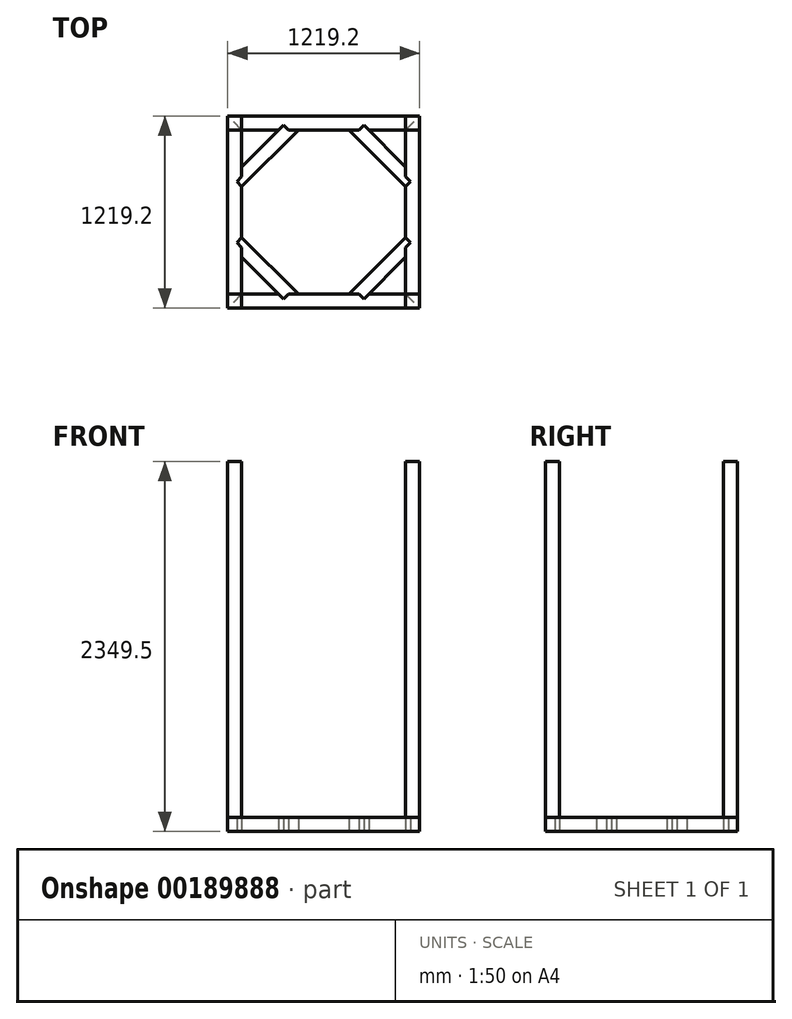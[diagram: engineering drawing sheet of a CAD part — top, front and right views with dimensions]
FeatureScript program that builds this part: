
annotation { "Feature Type Name" : "Feature", "Feature Type Description" : "" }
export const myFeature = defineFeature(function(context is Context, id is Id, definition is map)
    precondition{}
    {
        {
            var Q0;
            Q0=qCreatedBy(makeId("Top.planeOp"),FACE);
            var sketch = newSketch(context, id + "F0", { "sketchPlane" : qUnion([Q0])});
            skLineSegment(sketch, "E0.bottom", {"start": v(609.6, 609.6) * mm, "end": v(-609.6, 609.6) * mm});
            skLineSegment(sketch, "E0.top", {"start": v(609.6, -609.6) * mm, "end": v(-609.6, -609.6) * mm});
            skLineSegment(sketch, "E0.left", {"start": v(609.6, 609.6) * mm, "end": v(609.6, -609.6) * mm});
            skLineSegment(sketch, "E0.right", {"start": v(-609.6, 609.6) * mm, "end": v(-609.6, -609.6) * mm});
            skPoint(sketch, "E0.middle", {"position": v(0, 0) * mm});
            skLineSegment(sketch, "E1.0", {"start": v(520.7, 520.7) * mm, "end": v(287.21, 520.7) * mm});
            skLineSegment(sketch, "E1.1", {"start": v(520.7, 520.7) * mm, "end": v(520.7, 224.35) * mm});
            skLineSegment(sketch, "E1.2", {"start": v(520.7, -520.7) * mm, "end": v(287.21, -520.7) * mm});
            skLineSegment(sketch, "E1.3", {"start": v(-520.7, 520.7) * mm, "end": v(-520.7, 224.35) * mm});
            skLineSegment(sketch, "E2", {"start": v(-520.7, 520.7) * mm, "end": v(-609.6, 609.6) * mm});
            skLineSegment(sketch, "E3", {"start": v(520.7, 520.7) * mm, "end": v(609.6, 609.6) * mm});
            skLineSegment(sketch, "E4", {"start": v(520.7, -520.7) * mm, "end": v(609.6, -609.6) * mm});
            skLineSegment(sketch, "E5", {"start": v(-520.7, -520.7) * mm, "end": v(-609.6, -609.6) * mm});
            skLineSegment(sketch, "E6", {"start": v(-161.49, -520.7) * mm, "end": v(-520.7, -161.49) * mm});
            skLineSegment(sketch, "E7", {"start": v(-287.21, -520.7) * mm, "end": v(-520.7, -287.21) * mm});
            skLineSegment(sketch, "E8", {"start": v(-520.7, -161.49) * mm, "end": v(-552.13, -192.92) * mm});
            skLineSegment(sketch, "E9", {"start": v(-552.13, -192.92) * mm, "end": v(-520.7, -224.35) * mm});
            skLineSegment(sketch, "E10", {"start": v(-287.21, -520.7) * mm, "end": v(-255.78, -552.13) * mm});
            skLineSegment(sketch, "E11", {"start": v(-255.78, -552.13) * mm, "end": v(-224.35, -520.7) * mm});
            skLineSegment(sketch, "E12.trimOffspring", {"start": v(-287.21, -520.7) * mm, "end": v(-520.7, -520.7) * mm});
            skLineSegment(sketch, "E13.trimOffspring", {"start": v(-520.7, -224.35) * mm, "end": v(-520.7, -520.7) * mm});
            skLineSegment(sketch, "E14", {"start": v(0, 609.6) * mm, "end": v(0, -609.6) * mm, "construction": true});
            skLineSegment(sketch, "E15", {"start": v(609.6, 0) * mm, "end": v(-609.6, 0) * mm, "construction": true});
            skLineSegment(sketch, "E16.MirrorCS", {"start": v(161.49, -520.7) * mm, "end": v(520.7, -161.49) * mm});
            skLineSegment(sketch, "E17.MirrorCS", {"start": v(287.21, -520.7) * mm, "end": v(520.7, -287.21) * mm});
            skLineSegment(sketch, "E18.MirrorCS", {"start": v(552.13, -192.92) * mm, "end": v(520.7, -224.35) * mm});
            skLineSegment(sketch, "E19.MirrorCS", {"start": v(520.7, -161.49) * mm, "end": v(552.13, -192.92) * mm});
            skLineSegment(sketch, "E20.MirrorCS", {"start": v(255.78, -552.13) * mm, "end": v(224.35, -520.7) * mm});
            skLineSegment(sketch, "E21.MirrorCS", {"start": v(287.21, -520.7) * mm, "end": v(255.78, -552.13) * mm});
            skLineSegment(sketch, "E22.trimOffspring", {"start": v(224.35, -520.7) * mm, "end": v(-224.35, -520.7) * mm});
            skLineSegment(sketch, "E23.trimOffspring", {"start": v(520.7, -224.35) * mm, "end": v(520.7, -520.7) * mm});
            skLineSegment(sketch, "E24.MirrorCS", {"start": v(161.49, 520.7) * mm, "end": v(520.7, 161.49) * mm});
            skLineSegment(sketch, "E25.MirrorCS", {"start": v(520.7, 161.49) * mm, "end": v(552.13, 192.92) * mm});
            skLineSegment(sketch, "E26.MirrorCS", {"start": v(552.13, 192.92) * mm, "end": v(520.7, 224.35) * mm});
            skLineSegment(sketch, "E27.MirrorCS", {"start": v(287.21, 520.7) * mm, "end": v(520.7, 287.21) * mm});
            skLineSegment(sketch, "E28.MirrorCS", {"start": v(255.78, 552.13) * mm, "end": v(224.35, 520.7) * mm});
            skLineSegment(sketch, "E29.MirrorCS", {"start": v(287.21, 520.7) * mm, "end": v(255.78, 552.13) * mm});
            skLineSegment(sketch, "E30.MirrorCS", {"start": v(-161.49, 520.7) * mm, "end": v(-520.7, 161.49) * mm});
            skLineSegment(sketch, "E31.MirrorCS", {"start": v(-287.21, 520.7) * mm, "end": v(-520.7, 287.21) * mm});
            skLineSegment(sketch, "E32.MirrorCS", {"start": v(-552.13, 192.92) * mm, "end": v(-520.7, 224.35) * mm});
            skLineSegment(sketch, "E33.MirrorCS", {"start": v(-520.7, 161.49) * mm, "end": v(-552.13, 192.92) * mm});
            skLineSegment(sketch, "E34.MirrorCS", {"start": v(-287.21, 520.7) * mm, "end": v(-255.78, 552.13) * mm});
            skLineSegment(sketch, "E35.MirrorCS", {"start": v(-255.78, 552.13) * mm, "end": v(-224.35, 520.7) * mm});
            skLineSegment(sketch, "E36.trimOffspring", {"start": v(-287.21, 520.7) * mm, "end": v(-520.7, 520.7) * mm});
            skLineSegment(sketch, "E37.trimOffspring", {"start": v(-520.7, 161.49) * mm, "end": v(-520.7, -161.49) * mm});
            skLineSegment(sketch, "E38.trimOffspring", {"start": v(224.35, 520.7) * mm, "end": v(-224.35, 520.7) * mm});
            skLineSegment(sketch, "E39.trimOffspring", {"start": v(520.7, 161.49) * mm, "end": v(520.7, -161.49) * mm});
            skSolve(sketch);
        }
        {
            var Q0;
            Q0=makeQuery(id+"F0.imprint","IMPRINT",FACE,{"disambiguationData":[TD([[makeQuery(id+"F0.imprint","IMPRINT",EDGE,{"derivedFrom":sQuery(id+"F0.wireOp",EDGE,"E0.bottom")}),1.0]])]});
            extrude(context, id + "F1", {"entities" : qUnion([Q0]), "depth" : 88.9 * mm});
        }
        {
            var Q0;
            Q0=makeQuery(id+"F0.imprint","IMPRINT",FACE,{"disambiguationData":[TD([[makeQuery(id+"F0.imprint","IMPRINT",EDGE,{"derivedFrom":sQuery(id+"F0.wireOp",EDGE,"E0.right")}),1.0]])]});
            extrude(context, id + "F2", {"entities" : qUnion([Q0]), "depth" : 88.9 * mm});
        }
        {
            var Q0;
            Q0=makeQuery(id+"F0.imprint","IMPRINT",FACE,{"disambiguationData":[TD([[makeQuery(id+"F0.imprint","IMPRINT",EDGE,{"derivedFrom":sQuery(id+"F0.wireOp",EDGE,"E0.top")}),-1.0]])]});
            extrude(context, id + "F3", {"entities" : qUnion([Q0]), "depth" : 88.9 * mm});
        }
        {
            var Q0;
            Q0=makeQuery(id+"F0.imprint","IMPRINT",FACE,{"disambiguationData":[TD([[makeQuery(id+"F0.imprint","IMPRINT",EDGE,{"derivedFrom":sQuery(id+"F0.wireOp",EDGE,"E0.left")}),-1.0]])]});
            extrude(context, id + "F4", {"entities" : qUnion([Q0]), "depth" : 88.9 * mm});
        }
        {
            var Q0;
            {var subQ2=sQuery(id+"F0.wireOp",EDGE,"E30.MirrorCS");Q0=makeQuery(id+"F0.imprint","IMPRINT",FACE,{"disambiguationData":[TD([[makeQuery(id+"F0.imprint","IMPRINT",EDGE,{"derivedFrom":subQ2}),-1.0]])]});}
            extrude(context, id + "F5", {"entities" : qUnion([Q0]), "depth" : 88.9 * mm});
        }
        {
            var Q0;
            {var subQ1=sQuery(id+"F0.wireOp",EDGE,"E24.MirrorCS");Q0=makeQuery(id+"F0.imprint","IMPRINT",FACE,{"disambiguationData":[TD([[makeQuery(id+"F0.imprint","IMPRINT",EDGE,{"derivedFrom":subQ1}),1.0]])]});}
            extrude(context, id + "F6", {"entities" : qUnion([Q0]), "depth" : 88.9 * mm});
        }
        {
            var Q0;
            {var subQ2=sQuery(id+"F0.wireOp",EDGE,"E6");Q0=makeQuery(id+"F0.imprint","IMPRINT",FACE,{"disambiguationData":[TD([[makeQuery(id+"F0.imprint","IMPRINT",EDGE,{"derivedFrom":subQ2}),1.0]])]});}
            extrude(context, id + "F7", {"entities" : qUnion([Q0]), "depth" : 88.9 * mm});
        }
        {
            var Q0;
            {var subQ2=sQuery(id+"F0.wireOp",EDGE,"E16.MirrorCS");Q0=makeQuery(id+"F0.imprint","IMPRINT",FACE,{"disambiguationData":[TD([[makeQuery(id+"F0.imprint","IMPRINT",EDGE,{"derivedFrom":subQ2}),-1.0]])]});}
            extrude(context, id + "F8", {"entities" : qUnion([Q0]), "depth" : 88.9 * mm});
        }
        {
            var Q0;
            Q0=makeQuery(id+"F1.opExtrude","CAP_FACE",FACE,{"disambiguationData":[OSD([sQuery(id+"F0.wireOp",EDGE,"E0.bottom"),sQuery(id+"F0.wireOp",EDGE,"E1.0"),sQuery(id+"F0.wireOp",EDGE,"E2"),sQuery(id+"F0.wireOp",EDGE,"E3"),sQuery(id+"F0.wireOp",EDGE,"E28.MirrorCS"),sQuery(id+"F0.wireOp",EDGE,"E29.MirrorCS"),sQuery(id+"F0.wireOp",EDGE,"E34.MirrorCS"),sQuery(id+"F0.wireOp",EDGE,"E35.MirrorCS"),sQuery(id+"F0.wireOp",EDGE,"E36.trimOffspring"),sQuery(id+"F0.wireOp",EDGE,"E38.trimOffspring")])],"isStart":false});
            var sketch = newSketch(context, id + "F9", { "sketchPlane" : qUnion([Q0])});
            skLineSegment(sketch, "E40.bottom", {"start": v(-609.6, 609.6) * mm, "end": v(-520.7, 609.6) * mm});
            skLineSegment(sketch, "E40.top", {"start": v(-609.6, 520.7) * mm, "end": v(-520.7, 520.7) * mm});
            skLineSegment(sketch, "E40.left", {"start": v(-609.6, 609.6) * mm, "end": v(-609.6, 520.7) * mm});
            skLineSegment(sketch, "E40.right", {"start": v(-520.7, 609.6) * mm, "end": v(-520.7, 520.7) * mm});
            skLineSegment(sketch, "E41.bottom", {"start": v(609.6, 609.6) * mm, "end": v(520.7, 609.6) * mm});
            skLineSegment(sketch, "E41.top", {"start": v(609.6, 520.7) * mm, "end": v(520.7, 520.7) * mm});
            skLineSegment(sketch, "E41.left", {"start": v(609.6, 609.6) * mm, "end": v(609.6, 520.7) * mm});
            skLineSegment(sketch, "E41.right", {"start": v(520.7, 609.6) * mm, "end": v(520.7, 520.7) * mm});
            skPoint(sketch, "E42.0", {"position": v(609.6, -609.6) * mm});
            skPoint(sketch, "E43.0", {"position": v(-609.6, -609.6) * mm});
            skPoint(sketch, "E44.0", {"position": v(-520.7, -520.7) * mm});
            skPoint(sketch, "E45.0", {"position": v(520.7, -520.7) * mm});
            skLineSegment(sketch, "E46.bottom", {"start": v(-609.6, -609.6) * mm, "end": v(-520.7, -609.6) * mm});
            skLineSegment(sketch, "E46.top", {"start": v(-609.6, -520.7) * mm, "end": v(-520.7, -520.7) * mm});
            skLineSegment(sketch, "E46.left", {"start": v(-609.6, -609.6) * mm, "end": v(-609.6, -520.7) * mm});
            skLineSegment(sketch, "E46.right", {"start": v(-520.7, -609.6) * mm, "end": v(-520.7, -520.7) * mm});
            skLineSegment(sketch, "E47.bottom", {"start": v(609.6, -609.6) * mm, "end": v(520.7, -609.6) * mm});
            skLineSegment(sketch, "E47.top", {"start": v(609.6, -520.7) * mm, "end": v(520.7, -520.7) * mm});
            skLineSegment(sketch, "E47.left", {"start": v(609.6, -609.6) * mm, "end": v(609.6, -520.7) * mm});
            skLineSegment(sketch, "E47.right", {"start": v(520.7, -609.6) * mm, "end": v(520.7, -520.7) * mm});
            skSolve(sketch);
        }
        {
            var Q0;
            Q0=makeQuery(id+"F9.imprint","IMPRINT",FACE,{"disambiguationData":[TD([[makeQuery(id+"F9.imprint","IMPRINT",EDGE,{"derivedFrom":sQuery(id+"F9.wireOp",EDGE,"E40.bottom")}),1.0]])]});
            var Q1;
            Q1=makeQuery(id+"F9.imprint","IMPRINT",FACE,{"disambiguationData":[TD([[makeQuery(id+"F9.imprint","IMPRINT",EDGE,{"derivedFrom":sQuery(id+"F9.wireOp",EDGE,"E40.top")}),1.0]])]});
            extrude(context, id + "F10", {"entities" : qUnion([Q0, Q1]), "depth" : 2260.6 * mm});
        }
        {
            var Q0;
            Q0=makeQuery(id+"F9.imprint","IMPRINT",FACE,{"disambiguationData":[TD([[makeQuery(id+"F9.imprint","IMPRINT",EDGE,{"derivedFrom":sQuery(id+"F9.wireOp",EDGE,"E41.bottom")}),1.0]])]});
            var Q1;
            Q1=makeQuery(id+"F9.imprint","IMPRINT",FACE,{"disambiguationData":[TD([[makeQuery(id+"F9.imprint","IMPRINT",EDGE,{"derivedFrom":sQuery(id+"F9.wireOp",EDGE,"E41.top")}),-1.0]])]});
            extrude(context, id + "F11", {"entities" : qUnion([Q0, Q1]), "depth" : 2260.6 * mm});
        }
        {
            var Q0;
            Q0=makeQuery(id+"F9.imprint","IMPRINT",FACE,{"disambiguationData":[TD([[makeQuery(id+"F9.imprint","IMPRINT",EDGE,{"derivedFrom":sQuery(id+"F9.wireOp",EDGE,"E46.bottom")}),1.0]])]});
            extrude(context, id + "F12", {"entities" : qUnion([Q0]), "depth" : 2260.6 * mm});
        }
        {
            var Q0;
            Q0=makeQuery(id+"F9.imprint","IMPRINT",FACE,{"disambiguationData":[TD([[makeQuery(id+"F9.imprint","IMPRINT",EDGE,{"derivedFrom":sQuery(id+"F9.wireOp",EDGE,"E47.bottom")}),-1.0]])]});
            extrude(context, id + "F13", {"entities" : qUnion([Q0]), "depth" : 2260.6 * mm});
        }
    });
